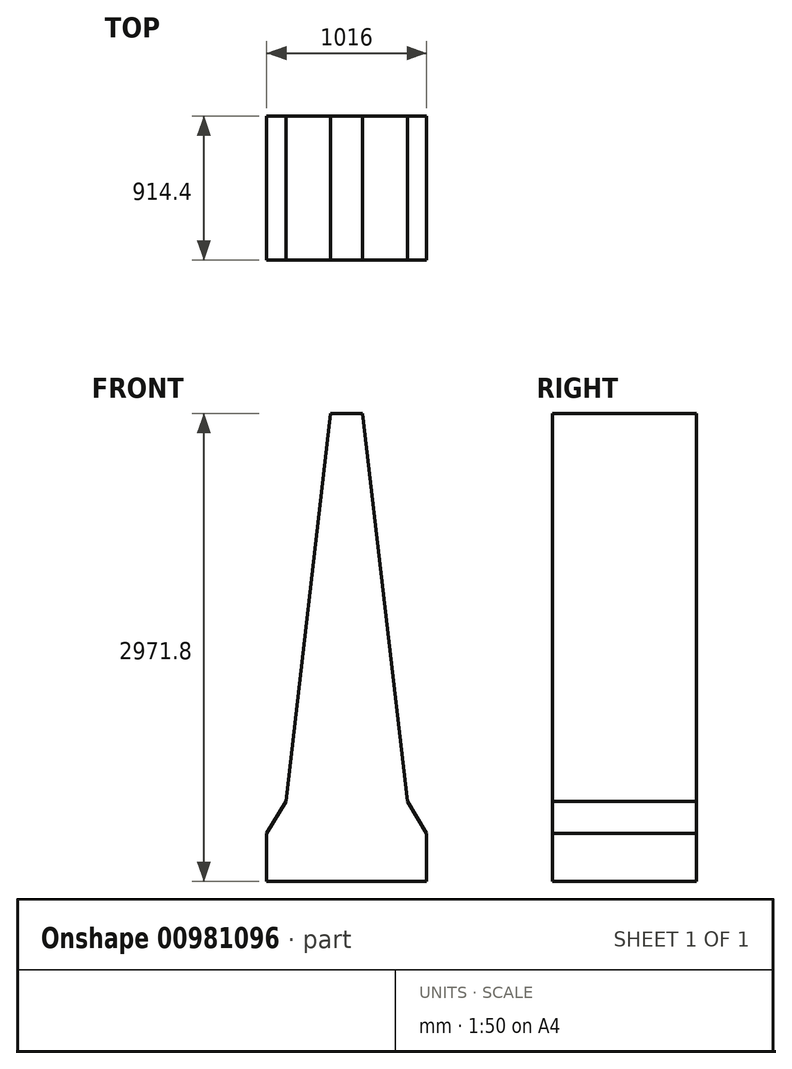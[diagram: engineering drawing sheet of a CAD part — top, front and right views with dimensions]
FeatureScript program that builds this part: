
annotation { "Feature Type Name" : "Feature", "Feature Type Description" : "" }
export const myFeature = defineFeature(function(context is Context, id is Id, definition is map)
    precondition{}
    {
        {
            var Q0;
            Q0=qCreatedBy(makeId("Front.planeOp"),FACE);
            var sketch = newSketch(context, id + "F0", { "sketchPlane" : qUnion([Q0])});
            skLineSegment(sketch, "E0", {"start": v(0, 0) * mm, "end": v(0, 2971.8) * mm, "construction": true});
            skLineSegment(sketch, "E1", {"start": v(0, 2971.8) * mm, "end": v(101.6, 2971.8) * mm});
            skLineSegment(sketch, "E2", {"start": v(101.6, 2971.8) * mm, "end": v(384.67, 508) * mm});
            skLineSegment(sketch, "E3", {"start": v(384.67, 508) * mm, "end": v(508, 304.8) * mm});
            skLineSegment(sketch, "E4", {"start": v(508, 304.8) * mm, "end": v(508, 0) * mm});
            skLineSegment(sketch, "E5", {"start": v(508, 0) * mm, "end": v(0, 0) * mm});
            skLineSegment(sketch, "E6.MirrorCS", {"start": v(-508, 304.8) * mm, "end": v(-508, 0) * mm});
            skLineSegment(sketch, "E7.MirrorCS", {"start": v(-508, 0) * mm, "end": v(0, 0) * mm});
            skLineSegment(sketch, "E8.MirrorCS", {"start": v(-384.67, 508) * mm, "end": v(-508, 304.8) * mm});
            skLineSegment(sketch, "E9.MirrorCS", {"start": v(0, 2971.8) * mm, "end": v(-101.6, 2971.8) * mm});
            skLineSegment(sketch, "E10.MirrorCS", {"start": v(-101.6, 2971.8) * mm, "end": v(-384.67, 508) * mm});
            skSolve(sketch);
        }
        {
            var Q0;
            Q0 = qSketchRegion(id + "F0", true);
            extrude(context, id + "F1", {"entities" : qUnion([Q0]), "endBound" : BoundingType.SYMMETRIC, "depth" : 914.4 * mm, "offsetDistance" : 25 * mm});
        }
    });
